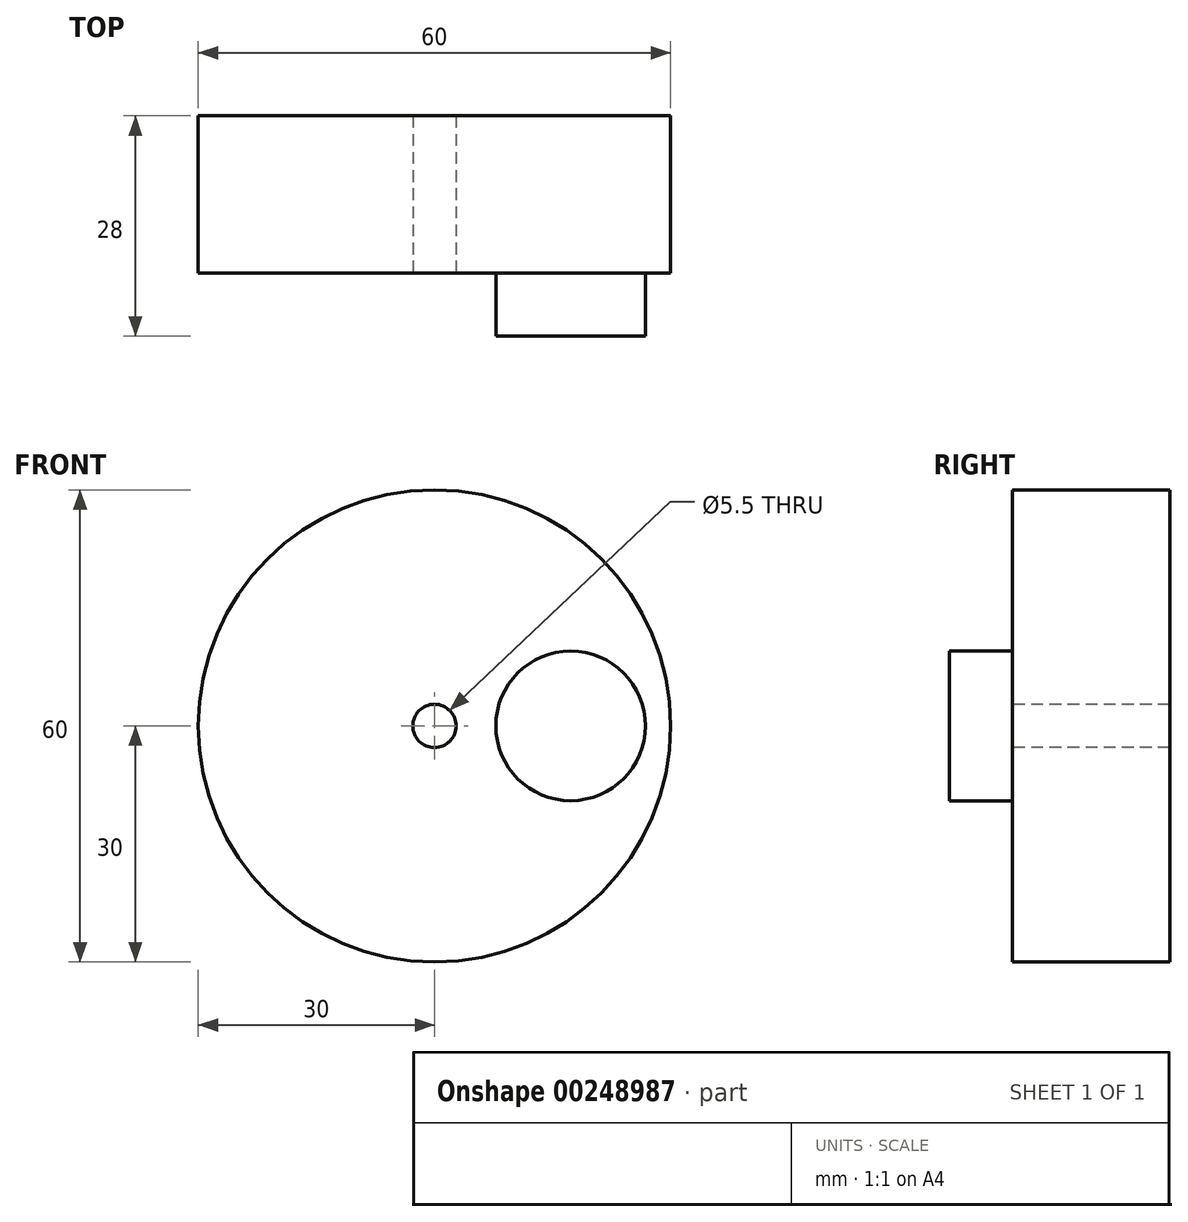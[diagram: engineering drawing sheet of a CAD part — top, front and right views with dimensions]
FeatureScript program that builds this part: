
annotation { "Feature Type Name" : "Feature", "Feature Type Description" : "" }
export const myFeature = defineFeature(function(context is Context, id is Id, definition is map)
    precondition{}
    {
        {
            var Q0;
            Q0=qCreatedBy(makeId("Front.planeOp"),FACE);
            var sketch = newSketch(context, id + "F0", { "sketchPlane" : qUnion([Q0])});
            skCircle(sketch, "E0", {"center": v(0, 0) * mm, "radius": 30 * mm});
            skPoint(sketch, "E1", {"position": v(17.3, 0) * mm});
            skCircle(sketch, "E2", {"center": v(17.3, 0) * mm, "radius": 9.5 * mm});
            skSolve(sketch);
        }
        {
            var Q0;
            Q0=makeQuery(id+"F0.imprint","IMPRINT",FACE,{"disambiguationData":[TD([[makeQuery(id+"F0.imprint","IMPRINT",EDGE,{"derivedFrom":sQuery(id+"F0.wireOp",EDGE,"E0")}),1.0]])]});
            var Q1;
            Q1=makeQuery(id+"F0.imprint","IMPRINT",FACE,{"disambiguationData":[TD([[makeQuery(id+"F0.imprint","IMPRINT",EDGE,{"derivedFrom":sQuery(id+"F0.wireOp",EDGE,"E2")}),1.0]])]});
            extrude(context, id + "F1", {"entities" : qUnion([Q0, Q1]), "oppositeDirection" : true, "depth" : 20 * mm});
        }
        {
            var Q0;
            Q0=makeQuery(id+"F0.imprint","IMPRINT",FACE,{"disambiguationData":[TD([[makeQuery(id+"F0.imprint","IMPRINT",EDGE,{"derivedFrom":sQuery(id+"F0.wireOp",EDGE,"E2")}),1.0]])]});
            extrude(context, id + "F2", {"entities" : qUnion([Q0]), "operationType" : NewBodyOperationType.ADD, "depth" : 8 * mm});
        }
        {
            var Q0;
            Q0=sQuery(id+"F0.wireOp",VERTEX,"E0.center");
            var Q1;
            Q1=makeQuery(id+"F1.opExtrude","SWEPT_BODY",BODY,{"disambiguationData":[OSD([sQuery(id+"F0.wireOp",EDGE,"E0")])]});
            hole(context, id + "F3", {"style" : HoleStyle.SIMPLE, "endStyle" : HoleEndStyle.THROUGH, "standardTappedOrClearance" : lookupTablePath({ "standard" : "ISO", "fit" : "Normal", "size" : "M5", "type" : "Clearance" }), "standardBlindInLast" : lookupTablePath({ "fit" : "Standard", "standard" : "ISO", "size" : "M5", "type" : "Clearance" }), "holeDiameter" : 5.5 * mm, "tappedDepth" : 11.6 * mm, "tapClearance" : 3, "startFromSketch" : true, "locations" : qUnion([Q0]), "scope" : qUnion([Q1])});
        }
    });
